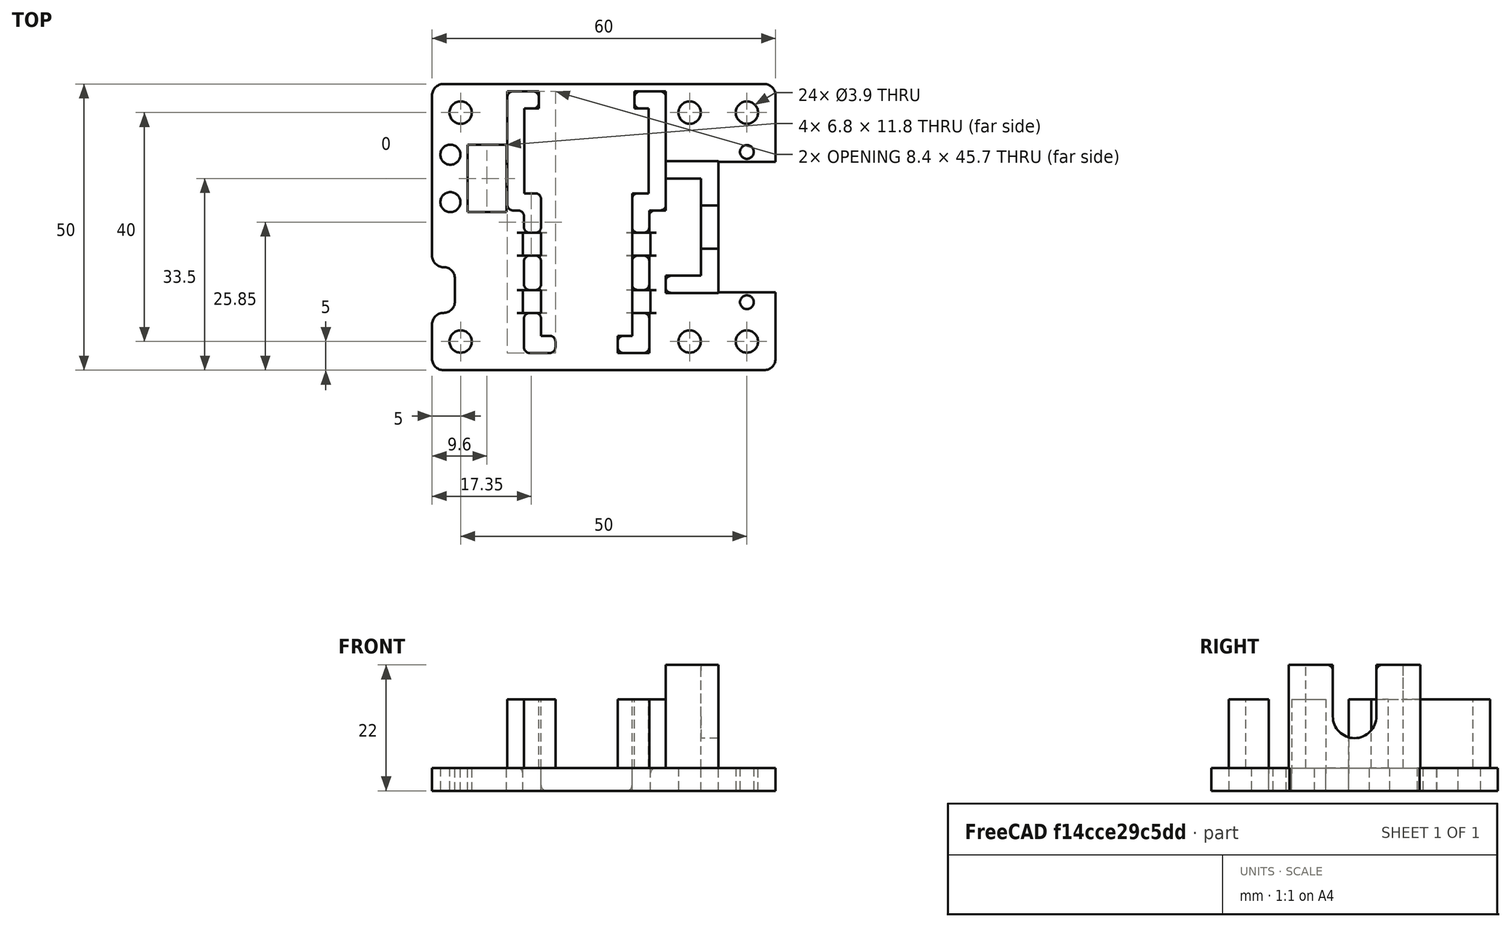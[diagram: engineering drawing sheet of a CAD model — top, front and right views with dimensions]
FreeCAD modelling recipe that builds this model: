
FCSTD DOCUMENT  (FreeCAD 1.0R39319 (Git))
Label: BottomHolder
License: All rights reserved
LicenseURL: https://en.wikipedia.org/wiki/All_rights_reserved
objects: Part::Fillet×47, Part::Part2DObjectPython×22, Part::Plane×20, Part::Fuse×8, Part::MultiFuse×7, Part::Cut×5, Part::FeaturePython×5, Part::Extrusion×5, Part::Box×3, Part::Mirroring×1
note: 123 computed .brp shape members not serialized (recipe doc carries the construction recipe); baked Part::Feature solids carry a one-line shape summary decoded from their .brp

FEATURE [Part::Plane] square
  AttacherType = Attacher::AttachEngine3D
  Length = 50
  Placement = pos=(-25,-25,0) rot=(0,0,1;0rad)
  Width = 50
FEATURE [Part::Part2DObjectPython] circle  # Draft 2D object (typed FeaturePython)
  Area = 11.9459
  FirstAngle = 0
  LastAngle = 0
  MakeFace = true
  Radius = 1.95
FEATURE [Part::Part2DObjectPython] Circle  # Draft 2D object (typed FeaturePython)
  Area = 11.9459
  FirstAngle = 0
  LastAngle = 0
  MakeFace = true
  Placement = pos=(-20,-20,0) rot=(0,0,1;0rad)
  Radius = 1.95
FEATURE [Part::Part2DObjectPython] circle001  # Draft 2D object (typed FeaturePython)
  Area = 11.9459
  FirstAngle = 0
  LastAngle = 0
  MakeFace = true
  Radius = 1.95
FEATURE [Part::Part2DObjectPython] Circle001  # Draft 2D object (typed FeaturePython)
  Area = 11.9459
  FirstAngle = 0
  LastAngle = 0
  MakeFace = true
  Placement = pos=(20,-20,0) rot=(0,0,1;0rad)
  Radius = 1.95
FEATURE [Part::Part2DObjectPython] circle002  # Draft 2D object (typed FeaturePython)
  Area = 11.9459
  FirstAngle = 0
  LastAngle = 0
  MakeFace = true
  Radius = 1.95
FEATURE [Part::Part2DObjectPython] Circle002  # Draft 2D object (typed FeaturePython)
  Area = 11.9459
  FirstAngle = 0
  LastAngle = 0
  MakeFace = true
  Placement = pos=(20,20,0) rot=(0,0,1;0rad)
  Radius = 1.95
FEATURE [Part::Part2DObjectPython] circle003  # Draft 2D object (typed FeaturePython)
  Area = 11.9459
  FirstAngle = 0
  LastAngle = 0
  MakeFace = true
  Radius = 1.95
FEATURE [Part::Part2DObjectPython] Circle003  # Draft 2D object (typed FeaturePython)
  Area = 11.9459
  FirstAngle = 0
  LastAngle = 0
  MakeFace = true
  Placement = pos=(-20,20,0) rot=(0,0,1;0rad)
  Radius = 1.95
FEATURE [Part::MultiFuse] Group
  Refine = true
  Shapes = -> [Circle,Circle001,Circle002,Circle003]
FEATURE [Part::Plane] square001
  AttacherType = Attacher::AttachEngine3D
  Length = 4
  Placement = pos=(-25,-15,0) rot=(0,0,1;0rad)
  Width = 8
FEATURE [Part::Plane] square002
  AttacherType = Attacher::AttachEngine3D
  Length = 6.8
  Placement = pos=(-18.8,2.6,0) rot=(0,0,1;0rad)
  Width = 11.8
FEATURE [Part::Part2DObjectPython] circle004  # Draft 2D object (typed FeaturePython)
  Area = 9.62113
  FirstAngle = 0
  LastAngle = 0
  MakeFace = true
  Radius = 1.75
FEATURE [Part::Part2DObjectPython] Circle004  # Draft 2D object (typed FeaturePython)
  Area = 9.62113
  FirstAngle = 0
  LastAngle = 0
  MakeFace = true
  Placement = pos=(-21.8,4.35,0) rot=(0,0,1;0rad)
  Radius = 1.75
FEATURE [Part::Part2DObjectPython] circle005  # Draft 2D object (typed FeaturePython)
  Area = 9.62113
  FirstAngle = 0
  LastAngle = 0
  MakeFace = true
  Radius = 1.75
FEATURE [Part::Part2DObjectPython] Circle005  # Draft 2D object (typed FeaturePython)
  Area = 9.62113
  FirstAngle = 0
  LastAngle = 0
  MakeFace = true
  Placement = pos=(-21.8,12.65,0) rot=(0,0,1;0rad)
  Radius = 1.75
FEATURE [Part::MultiFuse] Group001
  Refine = true
  Shapes = -> [square002,Circle004,Circle005]
FEATURE [Part::Fuse] union
  Base = -> square001
  Refine = true
  Tool = -> Group001
FEATURE [Part::Fuse] union001
  Base = -> Group
  Refine = true
  Tool = -> union
FEATURE [Part::Cut] difference
  Base = -> square
  Refine = true
  Tool = -> union001
FEATURE [Part::Plane] square003
  AttacherType = Attacher::AttachEngine3D
  Length = 10
  Placement = pos=(25,-25,0) rot=(0,0,1;0rad)
  Width = 50
FEATURE [Part::Part2DObjectPython] circle006  # Draft 2D object (typed FeaturePython)
  Area = 11.9459
  FirstAngle = 0
  LastAngle = 0
  MakeFace = true
  Radius = 1.95
FEATURE [Part::Part2DObjectPython] Circle006  # Draft 2D object (typed FeaturePython)
  Area = 11.9459
  FirstAngle = 0
  LastAngle = 0
  MakeFace = true
  Placement = pos=(30,20,0) rot=(0,0,1;0rad)
  Radius = 1.95
FEATURE [Part::Part2DObjectPython] circle007  # Draft 2D object (typed FeaturePython)
  Area = 11.9459
  FirstAngle = 0
  LastAngle = 0
  MakeFace = true
  Radius = 1.95
FEATURE [Part::Part2DObjectPython] Circle007  # Draft 2D object (typed FeaturePython)
  Area = 11.9459
  FirstAngle = 0
  LastAngle = 0
  MakeFace = true
  Placement = pos=(30,-20,0) rot=(0,0,1;0rad)
  Radius = 1.95
FEATURE [Part::Fuse] union002
  Base = -> Circle006
  Refine = true
  Tool = -> Circle007
FEATURE [Part::Cut] difference001
  Base = -> square003
  Refine = true
  Tool = -> union002
FEATURE [Part::Fuse] union003
  Base = -> difference
  Refine = true
  Tool = -> difference001
FEATURE [Part::Plane] square004
  AttacherType = Attacher::AttachEngine3D
  Length = 22.75
  Placement = pos=(-11.375,-5,0) rot=(0,0,1;0rad)
  Width = 10
FEATURE [Part::Part2DObjectPython] circle008  # Draft 2D object (typed FeaturePython)
  Area = 4.52389
  FirstAngle = 0
  LastAngle = 0
  MakeFace = true
  Radius = 1.2
FEATURE [Part::Part2DObjectPython] Circle008  # Draft 2D object (typed FeaturePython)
  Area = 4.52389
  FirstAngle = 0
  LastAngle = 0
  MakeFace = true
  Placement = pos=(-13.125,0,0) rot=(0,0,1;0rad)
  Radius = 1.2
FEATURE [Part::Part2DObjectPython] circle009  # Draft 2D object (typed FeaturePython)
  Area = 4.52389
  FirstAngle = 0
  LastAngle = 0
  MakeFace = true
  Radius = 1.2
FEATURE [Part::Part2DObjectPython] Circle009  # Draft 2D object (typed FeaturePython)
  Area = 4.52389
  FirstAngle = 0
  LastAngle = 0
  MakeFace = true
  Placement = pos=(13.125,0,0) rot=(0,0,1;0rad)
  Radius = 1.2
FEATURE [Part::Fuse] Group002
  Base = -> Circle008
  Refine = true
  Tool = -> Circle009
FEATURE [Part::Fuse] union004
  Base = -> square004
  Placement = pos=(30,0,0) rot=(0,0,1;1.5708rad)
  Refine = true
  Tool = -> Group002
FEATURE [Part::Cut] difference002
  Base = -> union003
  Refine = true
  Tool = -> union004
FEATURE [Part::FeaturePython] RefineLinearExtrude  # WARN: FeaturePython — macro-defined, semantics opaque (R4)
  Base = -> difference002
FEATURE [Part::Extrusion] LinearExtrude
  Base = -> RefineLinearExtrude
  Dir = (0,0,4)
  DirMode = 0
  FaceMakerClass = Part::FaceMakerBullseye
  FaceMakerMode = 3
  LengthFwd = 0
  LengthRev = 0
  Solid = false
  Symmetric = false
FEATURE [Part::Plane] square005
  AttacherType = Attacher::AttachEngine3D
  Length = 5.5
  Placement = pos=(-10.95,0,0) rot=(0,0,1;0rad)
  Width = 3
FEATURE [Part::Plane] square006
  AttacherType = Attacher::AttachEngine3D
  Length = 5.5
  Placement = pos=(-13.85,42.7,0) rot=(0,0,1;0rad)
  Width = 3
FEATURE [Part::Plane] square007
  AttacherType = Attacher::AttachEngine3D
  Length = 2.9
  Placement = pos=(-13.85,24.9,0) rot=(0,0,1;0rad)
  Width = 3
FEATURE [Part::Plane] square008
  AttacherType = Attacher::AttachEngine3D
  Length = 3
  Placement = pos=(-10.95,3,0) rot=(0,0,1;0rad)
  Width = 24.9
FEATURE [Part::Plane] square009
  AttacherType = Attacher::AttachEngine3D
  Length = 3
  Placement = pos=(-13.85,27.9,0) rot=(0,0,1;0rad)
  Width = 14.8
FEATURE [Part::MultiFuse] union005
  Refine = true
  Shapes = -> [square005,square006,square007,square008,square009]
FEATURE [Part::FeaturePython] RefineLinearExtrude001  # WARN: FeaturePython — macro-defined, semantics opaque (R4)
  Base = -> union005
FEATURE [Part::Extrusion] LinearExtrude001
  Base = -> RefineLinearExtrude001
  Dir = (0,0,12)
  DirMode = 0
  FaceMakerClass = Part::FaceMakerBullseye
  FaceMakerMode = 3
  LengthFwd = 0
  LengthRev = 0
  Solid = false
  Symmetric = false
FEATURE [Part::Plane] square010
  AttacherType = Attacher::AttachEngine3D
  Length = 5.5
  Placement = pos=(-10.95,0,0) rot=(0,0,1;0rad)
  Width = 3
FEATURE [Part::Plane] square011
  AttacherType = Attacher::AttachEngine3D
  Length = 5.5
  Placement = pos=(-13.85,42.7,0) rot=(0,0,1;0rad)
  Width = 3
FEATURE [Part::Plane] square012
  AttacherType = Attacher::AttachEngine3D
  Length = 2.9
  Placement = pos=(-13.85,24.9,0) rot=(0,0,1;0rad)
  Width = 3
FEATURE [Part::Plane] square013
  AttacherType = Attacher::AttachEngine3D
  Length = 3
  Placement = pos=(-10.95,3,0) rot=(0,0,1;0rad)
  Width = 24.9
FEATURE [Part::Plane] square014
  AttacherType = Attacher::AttachEngine3D
  Length = 3
  Placement = pos=(-13.85,27.9,0) rot=(0,0,1;0rad)
  Width = 14.8
FEATURE [Part::MultiFuse] union006
  Refine = true
  Shapes = -> [square010,square011,square012,square013,square014]
FEATURE [Part::FeaturePython] RefineLinearExtrude002  # WARN: FeaturePython — macro-defined, semantics opaque (R4)
  Base = -> union006
FEATURE [Part::Extrusion] LinearExtrude002
  Base = -> RefineLinearExtrude002
  Dir = (0,0,12)
  DirMode = 0
  FaceMakerClass = Part::FaceMakerBullseye
  FaceMakerMode = 3
  LengthFwd = 0
  LengthRev = 0
  Solid = false
  Symmetric = false
FEATURE [Part::Mirroring] mirr_LinearExtrude002  label="mirrored LinearExtrude002"
  Base = (0,0,0)
  Normal = (1,0,0)
  Source = -> LinearExtrude002
FEATURE [Part::Fuse] union007
  Base = -> LinearExtrude001
  Placement = pos=(2,-22,4) rot=(0,0,1;0rad)
  Refine = true
  Tool = -> mirr_LinearExtrude002
FEATURE [Part::Box] cube
  AttacherType = Attacher::AttachEngine3D
  Height = 18
  Length = 17
  Placement = pos=(-8.5,0,0) rot=(0,0,1;0rad)
  Width = 3
FEATURE [Part::Box] cube001
  AttacherType = Attacher::AttachEngine3D
  Height = 18
  Length = 3
  Placement = pos=(8.5,0,0) rot=(0,0,1;0rad)
  Width = 9.2
FEATURE [Part::Box] cube002
  AttacherType = Attacher::AttachEngine3D
  Height = 18
  Length = 3
  Placement = pos=(-11.5,0,0) rot=(0,0,1;0rad)
  Width = 9.2
FEATURE [Part::MultiFuse] union008
  Refine = true
  Shapes = -> [cube,cube001,cube002]
FEATURE [Part::Part2DObjectPython] circle010  # Draft 2D object (typed FeaturePython)
  Area = 45.3646
  FirstAngle = 0
  LastAngle = 0
  MakeFace = true
  Radius = 3.8
FEATURE [Part::Part2DObjectPython] Circle010  # Draft 2D object (typed FeaturePython)
  Area = 45.3646
  FirstAngle = 0
  LastAngle = 0
  MakeFace = true
  Placement = pos=(0,9,0) rot=(0,0,1;0rad)
  Radius = 3.8
FEATURE [Part::Plane] square015
  AttacherType = Attacher::AttachEngine3D
  Length = 7.6
  Placement = pos=(-3.8,9,0) rot=(0,0,1;0rad)
  Width = 9
FEATURE [Part::Fuse] union009
  Base = -> Circle010
  Refine = true
  Tool = -> square015
FEATURE [Part::FeaturePython] RefineLinearExtrude003  # WARN: FeaturePython — macro-defined, semantics opaque (R4)
  Base = -> union009
FEATURE [Part::Extrusion] LinearExtrude003
  Base = -> RefineLinearExtrude003
  Dir = (0,0,3.2)
  DirMode = 0
  FaceMakerClass = Part::FaceMakerBullseye
  FaceMakerMode = 3
  LengthFwd = 0
  LengthRev = 0
  Placement = pos=(0,3.1,0) rot=(1,0,0;1.5708rad)
  Solid = false
  Symmetric = false
FEATURE [Part::Cut] difference003
  Base = -> union008
  Placement = pos=(25,0,4) rot=(0,0,1;1.5708rad)
  Refine = true
  Tool = -> LinearExtrude003
FEATURE [Part::MultiFuse] union010
  Refine = true
  Shapes = -> [LinearExtrude,union007,difference003]
FEATURE [Part::Plane] square016
  AttacherType = Attacher::AttachEngine3D
  Length = 3.2
  Placement = pos=(-11.15,-15,0) rot=(0,0,1;0rad)
  Width = 4
FEATURE [Part::Plane] square017
  AttacherType = Attacher::AttachEngine3D
  Length = 3.2
  Placement = pos=(-11.15,-5,0) rot=(0,0,1;0rad)
  Width = 4
FEATURE [Part::Plane] square018
  AttacherType = Attacher::AttachEngine3D
  Length = 3.2
  Placement = pos=(7.95,-15,0) rot=(0,0,1;0rad)
  Width = 4
FEATURE [Part::Plane] square019
  AttacherType = Attacher::AttachEngine3D
  Length = 3.2
  Placement = pos=(7.95,-5,0) rot=(0,0,1;0rad)
  Width = 4
FEATURE [Part::MultiFuse] Group003
  Placement = pos=(2,0,0) rot=(0,0,1;0rad)
  Refine = true
  Shapes = -> [square016,square017,square018,square019]
FEATURE [Part::FeaturePython] RefineLinearExtrude004  # WARN: FeaturePython — macro-defined, semantics opaque (R4)
  Base = -> Group003
FEATURE [Part::Extrusion] LinearExtrude004
  Base = -> RefineLinearExtrude004
  Dir = (0,0,16)
  DirMode = 0
  FaceMakerClass = Part::FaceMakerBullseye
  FaceMakerMode = 3
  LengthFwd = 0
  LengthRev = 0
  Solid = false
  Symmetric = false
FEATURE [Part::Cut] difference004
  Base = -> union010
  Refine = true
  Tool = -> LinearExtrude004
FEATURE [Part::Fillet] Fillet
  Base = -> difference004
  EdgeLinks = -> difference004 [Edge1]
  Edges = 1 edges r=2: [Edge1]
FEATURE [Part::Fillet] Fillet001
  Base = -> Fillet
  EdgeLinks = -> Fillet [Edge3]
  Edges = 1 edges r=2: [Edge3]
FEATURE [Part::Fillet] Fillet002
  Base = -> Fillet001
  EdgeLinks = -> Fillet001 [Edge137]
  Edges = 1 edges r=2: [Edge137]
FEATURE [Part::Fillet] Fillet003
  Base = -> Fillet002
  EdgeLinks = -> Fillet002 [Edge51]
  Edges = 1 edges r=1.99: [Edge51]
FEATURE [Part::Fillet] Fillet004
  Base = -> Fillet003
  EdgeLinks = -> Fillet003 [Edge48]
  Edges = 1 edges r=1.99: [Edge48]
FEATURE [Part::Fillet] Fillet005
  Base = -> Fillet004
  EdgeLinks = -> Fillet004 [Edge63]
  Edges = 1 edges r=2: [Edge63]
FEATURE [Part::Fillet] Fillet006
  Base = -> Fillet005
  EdgeLinks = -> Fillet005 [Edge84]
  Edges = 1 edges r=2: [Edge84]
FEATURE [Part::Fillet] Fillet007
  Base = -> Fillet006
  EdgeLinks = -> Fillet006 [Edge75]
  Edges = 1 edges r=2: [Edge75]
FEATURE [Part::Fillet] Fillet008
  Base = -> Fillet007
  EdgeLinks = -> Fillet007 [Edge272]
  Edges = 1 edges r=1: [Edge272]
FEATURE [Part::Fillet] Fillet009
  Base = -> Fillet008
  EdgeLinks = -> Fillet008 [Edge93]
  Edges = 1 edges r=1: [Edge93]
FEATURE [Part::Fillet] Fillet010
  Base = -> Fillet009
  EdgeLinks = -> Fillet009 [Edge100]
  Edges = 1 edges r=1: [Edge100]
FEATURE [Part::Fillet] Fillet011
  Base = -> Fillet010
  EdgeLinks = -> Fillet010 [Edge112]
  Edges = 1 edges r=1: [Edge112]
FEATURE [Part::Fillet] Fillet012
  Base = -> Fillet011
  EdgeLinks = -> Fillet011 [Edge104]
  Edges = 1 edges r=1: [Edge104]
FEATURE [Part::Fillet] Fillet013
  Base = -> Fillet012
  EdgeLinks = -> Fillet012 [Edge118]
  Edges = 1 edges r=1: [Edge118]
FEATURE [Part::Fillet] Fillet014
  Base = -> Fillet013
  EdgeLinks = -> Fillet013 [Edge109]
  Edges = 1 edges r=1: [Edge109]
FEATURE [Part::Fillet] Fillet015
  Base = -> Fillet014
  EdgeLinks = -> Fillet014 [Edge103,Edge109,Edge121,Edge123]
  Edges = 4 edges r=1: [Edge103,Edge109,Edge121,Edge123]
FEATURE [Part::Fillet] Fillet016
  Base = -> Fillet015
  EdgeLinks = -> Fillet015 [Edge145,Edge149]
  Edges = 2 edges r=1: [Edge145,Edge149]
FEATURE [Part::Fillet] Fillet017
  Base = -> Fillet016
  EdgeLinks = -> Fillet016 [Edge149]
  Edges = 1 edges r=1: [Edge149]
FEATURE [Part::Fillet] Fillet018
  Base = -> Fillet016
  EdgeLinks = -> Fillet016 [Edge149]
  Edges = 1 edges r=1: [Edge149]
FEATURE [Part::Fillet] Fillet019
  Base = -> Fillet016
  EdgeLinks = -> Fillet016 [Edge149]
  Edges = 1 edges r=1: [Edge149]
FEATURE [Part::Fillet] Fillet020
  Base = -> Fillet017
  EdgeLinks = -> Fillet017 [Edge303,Edge312]
  Edges = 2 edges r=1: [Edge303,Edge312]
FEATURE [Part::Fillet] Fillet021
  Base = -> Fillet020
  EdgeLinks = -> Fillet020 [Edge125]
  Edges = 1 edges r=1: [Edge125]
FEATURE [Part::Fillet] Fillet022
  Base = -> Fillet020
  EdgeLinks = -> Fillet020 [Edge125]
  Edges = 1 edges r=1: [Edge125]
FEATURE [Part::Fillet] Fillet023
  Base = -> Fillet021
  EdgeLinks = -> Fillet021 [Edge215]
  Edges = 1 edges r=1: [Edge215]
FEATURE [Part::Fillet] Fillet024
  Base = -> Fillet023
  EdgeLinks = -> Fillet023 [Edge128,Edge130,Edge183]
  Edges = 3 edges r=1: [Edge128,Edge130,Edge183]
FEATURE [Part::Fillet] Fillet025
  Base = -> Fillet024
  EdgeLinks = -> Fillet024 [Edge164]
  Edges = 1 edges r=1: [Edge164]
FEATURE [Part::Fillet] Fillet026
  Base = -> Fillet025
  EdgeLinks = -> Fillet025 [Edge147]
  Edges = 1 edges r=1: [Edge147]
FEATURE [Part::Fillet] Fillet027
  Base = -> Fillet026
  EdgeLinks = -> Fillet026 [Edge156]
  Edges = 1 edges r=1: [Edge156]
FEATURE [Part::Fillet] Fillet028
  Base = -> Fillet027
  EdgeLinks = -> Fillet027 [Edge196,Edge200]
  Edges = 2 edges r=1: [Edge196,Edge200]
FEATURE [Part::Fillet] Fillet029
  Base = -> Fillet028
  EdgeLinks = -> Fillet028 [Edge133]
  Edges = 1 edges r=1: [Edge133]
FEATURE [Part::Fillet] Fillet030
  Base = -> Fillet029
  EdgeLinks = -> Fillet029 [Edge17]
  Edges = 1 edges r=1: [Edge17]
FEATURE [Part::Fillet] Fillet031
  Base = -> Fillet029
  EdgeLinks = -> Fillet029 [Edge17]
  Edges = 1 edges r=1: [Edge17]
FEATURE [Part::Fillet] Fillet032
  Base = -> Fillet030
  EdgeLinks = -> Fillet030 [Edge193]
  Edges = 1 edges r=1: [Edge193]
FEATURE [Part::Fillet] Fillet033
  Base = -> Fillet032
  EdgeLinks = -> Fillet032 [Edge174]
  Edges = 1 edges r=1: [Edge174]
FEATURE [Part::Fillet] Fillet034
  Base = -> Fillet033
  EdgeLinks = -> Fillet033 [Edge38]
  Edges = 1 edges r=1: [Edge38]
FEATURE [Part::Fillet] Fillet035
  Base = -> Fillet034
  EdgeLinks = -> Fillet034 [Edge45]
  Edges = 1 edges r=1: [Edge45]
FEATURE [Part::Fillet] Fillet036
  Base = -> Fillet035
  EdgeLinks = -> Fillet035 [Edge414]
  Edges = 1 edges r=1: [Edge414]
FEATURE [Part::Fillet] Fillet037
  Base = -> Fillet036
  EdgeLinks = -> Fillet036 [Edge137,Edge141]
  Edges = 2 edges r=1: [Edge137,Edge141]
FEATURE [Part::Fillet] Fillet038
  Base = -> Fillet037
  EdgeLinks = -> Fillet037 [Edge358,Edge362]
  Edges = 2 edges r=1: [Edge358,Edge362]
FEATURE [Part::Fillet] Fillet039
  Base = -> Fillet038
  EdgeLinks = -> Fillet038 [Edge155]
  Edges = 1 edges r=1: [Edge155]
FEATURE [Part::Fillet] Fillet040
  Base = -> Fillet039
  EdgeLinks = -> Fillet039 [Edge435]
  Edges = 1 edges r=1: [Edge435]
FEATURE [Part::Fillet] Fillet041
  Base = -> Fillet040
  EdgeLinks = -> Fillet040 [Edge169]
  Edges = 1 edges r=1: [Edge169]
FEATURE [Part::Fillet] Fillet042
  Base = -> Fillet041
  EdgeLinks = -> Fillet041 [Edge28]
  Edges = 1 edges r=1: [Edge28]
FEATURE [Part::Fillet] Fillet043
  Base = -> Fillet042
  EdgeLinks = -> Fillet042 [Edge10]
  Edges = 1 edges r=1: [Edge10]
FEATURE [Part::Fillet] Fillet044
  Base = -> Fillet043
  EdgeLinks = -> Fillet043 [Edge59]
  Edges = 1 edges r=1: [Edge59]
FEATURE [Part::Fillet] Fillet045
  Base = -> Fillet044
  EdgeLinks = -> Fillet044 [Edge102]
  Edges = 1 edges r=1: [Edge102]
FEATURE [Part::Fillet] Fillet046
  Base = -> Fillet045
  EdgeLinks = -> Fillet045 [Edge21]
  Edges = 1 edges r=1: [Edge21]
